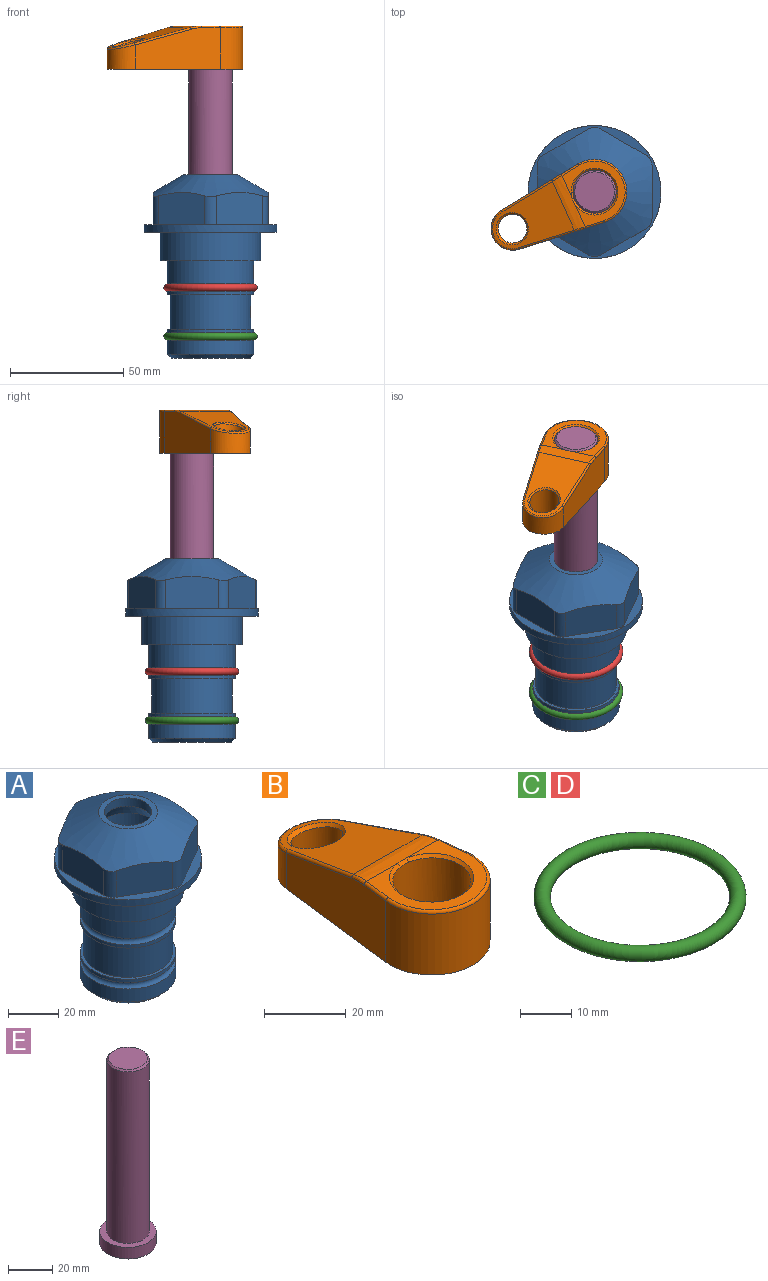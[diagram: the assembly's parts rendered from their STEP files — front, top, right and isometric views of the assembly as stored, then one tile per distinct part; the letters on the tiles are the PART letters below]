
ASSEMBLY  parts=5 mates=4
PART A: 36 faces, bbox 58.7x58.7x81 mm
  f0: cylinder r=17.78mm len=35.56mm, axis (0,0,1), area 1670.8mm2, adj f23,f24,f31
  f1: cylinder r=19.05mm len=38.1mm, axis (0,0,1), area 1191.9mm2, adj f26,f27,f30
  f2: plane 58.66x58.66mm, normal (0,0,-1), area 1150.6mm2, adj f3,f28
  f3: cylinder r=29.33mm len=58.66mm, axis (0,0,-1), area 585.1mm2, adj f2,f4
  f4: plane 58.66x58.66mm, normal (0,0,1), area 475.9mm2, adj f3,f5,f6,f7,f8,f9,f10,f11
  f5: plane 20.32x14.34mm, normal (-0.5,0.87,0), area 324.4mm2, adj f4,f15,f16,f17
  f6: plane 20.32x14.34mm, normal (0.5,0.87,0), area 324.4mm2, adj f4,f14,f15,f17
  f7: plane 23.48x14.34mm, normal (1,0,0), area 324.4mm2, adj f4,f13,f14,f17
  f8: plane 20.32x14.34mm, normal (0.5,-0.87,0), area 324.4mm2, adj f4,f12,f13,f17
  f9: plane 20.32x14.34mm, normal (-0.5,-0.87,0), area 324.4mm2, adj f4,f11,f12,f17
  f10: plane 23.48x14.34mm, normal (-1,0,0), area 324.4mm2, adj f4,f11,f16,f17
  f11: cylinder r=5.08mm len=12.85mm, axis (0,0,-1), area 67.2mm2, adj f4,f9,f10,f17
  f12: cylinder r=5.08mm len=12.85mm, axis (0,0,-1), area 67.2mm2, adj f4,f8,f9,f17
  f13: cylinder r=5.08mm len=12.85mm, axis (0,0,-1), area 67.2mm2, adj f4,f7,f8,f17
  f14: cylinder r=5.08mm len=12.85mm, axis (0,0,-1), area 67.2mm2, adj f4,f6,f7,f17
  f15: cylinder r=5.08mm len=12.85mm, axis (0,0,-1), area 67.2mm2, adj f4,f5,f6,f17
  f16: cylinder r=5.08mm len=12.85mm, axis (0,0,-1), area 67.2mm2, adj f4,f5,f10,f17
  f17: cone r=11.73mm half-angle=60deg, axis (0,0,-1), area 2071.8mm2, adj f5,f6,f7,f8,f9,f10,f11,f12
  f18: plane 23.46x23.46mm, normal (0,0,1), area 147.4mm2, adj f17,f35
  f19: plane 34.93x34.93mm, normal (0,0,-1), area 958mm2, adj f29
  f20: cylinder r=19.05mm len=38.1mm, axis (0,0,1), area 760.1mm2, adj f21,f29
  f21: torus R=19.05mm, axis (0,0,1), area 565.3mm2, adj f20,f22
  f22: cylinder r=19.05mm len=38.1mm, axis (0,0,1), area 190mm2, adj f21,f23
  f23: plane 38.1x38.1mm, normal (0,0,1), area 146.9mm2, adj f0,f22
  f24: plane 38.1x38.1mm, normal (0,0,-1), area 146.9mm2, adj f0,f25
  f25: cylinder r=19.05mm len=38.1mm, axis (0,0,1), area 190mm2, adj f24,f26
  f26: torus R=19.05mm, axis (0,0,1), area 565.3mm2, adj f1,f25
  f27: plane 44.45x44.45mm, normal (0,0,-1), area 411.7mm2, adj f1,f28
  f28: cylinder r=22.23mm len=44.45mm, axis (0,0,1), area 1773.5mm2, adj f2,f27
  f29: cone r=19.05mm half-angle=45deg, axis (0,0,1), area 257.5mm2, adj f19,f20
  f30: cylinder r=3.17mm len=6.75mm, axis (-1,0,0), area 128mm2, adj f1,f33
  f31: cylinder r=3.17mm len=6.35mm, axis (-1,0,0), area 102.5mm2, adj f0,f33
  f32: plane 25.4x25.4mm, normal (0,0,1), area 506.7mm2, adj f33
  f33: cylinder r=12.7mm len=66.42mm, axis (0,0,-1), area 5236.2mm2, adj f30,f31,f32,f34
  f34: cone r=9.53mm half-angle=30deg, axis (0,0,-1), area 443.4mm2, adj f33,f35
  f35: cylinder r=9.53mm len=19.05mm, axis (0,0,-1), area 240.9mm2, adj f18,f34
PART B: 31 faces, bbox 31.7x65.5x19.8 mm
  f0: plane 39.12x18.26mm, normal (0.99,0.12,0), area 612.2mm2, adj f1,f4,f7,f11,f13,f15
  f1: cylinder r=9.53mm len=18.91mm, axis (0,0,-1), area 296.1mm2, adj f0,f2,f7,f17
  f2: plane 39.12x18.26mm, normal (-0.99,0.12,0), area 612.2mm2, adj f1,f4,f7,f12,f14,f16
  f3: cylinder r=6.35mm len=12.7mm, axis (0,0,-1), area 362.4mm2, adj f7,f18
  f4: cylinder r=14.29mm len=28.58mm, axis (0,0,-1), area 882.2mm2, adj f0,f2,f7,f10
  f5: cylinder r=9.53mm len=19.05mm, axis (0,0,-1), area 1092.6mm2, adj f7,f19,f20
  f6: plane 26.99x23.69mm, normal (0,0,1), area 216.2mm2, adj f9,f10,f11,f12,f19
  f7: plane 63.5x28.58mm, normal (0,0,-1), area 661.8mm2, adj f0,f1,f2,f3,f4,f5,f22,f23
  f8: plane 33.52x23.6mm, normal (0,0.26,0.97), area 486mm2, adj f9,f15,f16,f17,f18
  f9: cylinder r=19.05mm len=24.72mm, axis (1,0,0), area 120.4mm2, adj f6,f8,f13,f14,f20
  f10: torus R=13.49mm, axis (0,0,1), area 59mm2, adj f4,f6,f11,f12
  f11: cylinder r=0.79mm len=8.67mm, axis (0.12,-0.99,0), area 10.8mm2, adj f0,f6,f10,f13
  f12: cylinder r=0.79mm len=8.67mm, axis (0.12,0.99,0), area 10.8mm2, adj f2,f6,f10,f14
  f13: bspline ~4.95x1.42mm, area 6.1mm2, adj f0,f9,f11,f15
  f14: bspline ~4.95x1.42mm, area 6.1mm2, adj f2,f9,f12,f16
  f15: cylinder r=0.79mm len=25.95mm, axis (0.12,-0.96,0.26), area 32.9mm2, adj f0,f8,f13,f17
  f16: cylinder r=0.79mm len=25.95mm, axis (0.12,0.96,-0.26), area 32.9mm2, adj f2,f8,f14,f17
  f17: bspline ~18.91x8.38mm, area 30mm2, adj f1,f8,f15,f16
  f18: bspline ~14.29x14.29mm, area 48.3mm2, adj f3,f8
  f19: cone r=9.53mm half-angle=45deg, axis (0,0,1), area 66.5mm2, adj f5,f6,f20
  f20: bspline ~3.22x0.96mm, area 3.5mm2, adj f5,f9,f19
  f21: plane 2.75x2.72mm, normal (0,0,-1), area 2.9mm2, adj f23,f25,f28
  f22: plane 23.05x15.88mm, normal (-0.99,-0.12,0), area 323.6mm2, adj f7,f25,f26,f27,f28,f29
  f23: plane 23.05x15.88mm, normal (0.99,-0.12,0), area 323.6mm2, adj f7,f21,f25,f27,f28,f30
  f24: cylinder r=9.53mm len=10.69mm, axis (0,0,-1), area 114.7mm2, adj f7,f27,f29,f30
  f25: cylinder r=12.7mm len=20.59mm, axis (0,0,-1), area 381.1mm2, adj f7,f21,f22,f23,f26,f28
  f26: plane 2.75x2.72mm, normal (0,0,-1), area 2.9mm2, adj f22,f25,f28
  f27: plane 19.72x18.37mm, normal (0,-0.26,-0.97), area 291.8mm2, adj f22,f23,f24,f28,f29,f30
  f28: cylinder r=15.88mm len=19.92mm, axis (1,0,0), area 54.8mm2, adj f21,f22,f23,f25,f26,f27
  f29: cylinder r=1.59mm len=11mm, axis (0,0,-1), area 34.7mm2, adj f7,f22,f24,f27
  f30: cylinder r=1.59mm len=11mm, axis (0,0,-1), area 34.7mm2, adj f7,f23,f24,f27
PART C: 1 faces, bbox 44.7x44.7x3.2 mm
  f0: torus R=19.05mm, axis (0,0,1), area 1193.9mm2
PART D: same geometry as C
PART E: 6 faces, bbox 25.4x25.4x101.6 mm
  f0: plane 17.46x17.46mm, normal (0,0,1), area 239.5mm2, adj f5
  f1: plane 25.4x25.4mm, normal (0,0,-1), area 506.7mm2, adj f2
  f2: cylinder r=12.7mm len=25.4mm, axis (0,0,1), area 506.7mm2, adj f1,f3
  f3: plane 25.4x25.4mm, normal (0,0,1), area 221.7mm2, adj f2,f4
  f4: cylinder r=9.53mm len=94.46mm, axis (0,0,1), area 5653mm2, adj f3,f5
  f5: cone r=8.73mm half-angle=45deg, axis (0,0,-1), area 64.4mm2, adj f0,f4
PLACE A at identity fixed
PLACE B rot(axis=(0,0,1),114.3deg) t=(0,0,27.55)mm
PLACE C t=(0,0,-21.59)mm
PLACE D at identity
PLACE E rot(axis=(0,0,1),114.3deg) t=(0,0,27.55)mm
MATE fastened B.f4 <-> E.f2  axis (0,0,1) through (0,0,91.05)mm
MATE cylindrical A.f0 <-> E.f2  axis (0,0,1) through (0,0,-50.55)mm
MATE fastened D.f0 <-> A.f0  axis (0,0,1) through (0,0,-24.51)mm
MATE fastened C.f0 <-> A.f0  axis (0,0,1) through (0,0,-46.1)mm
